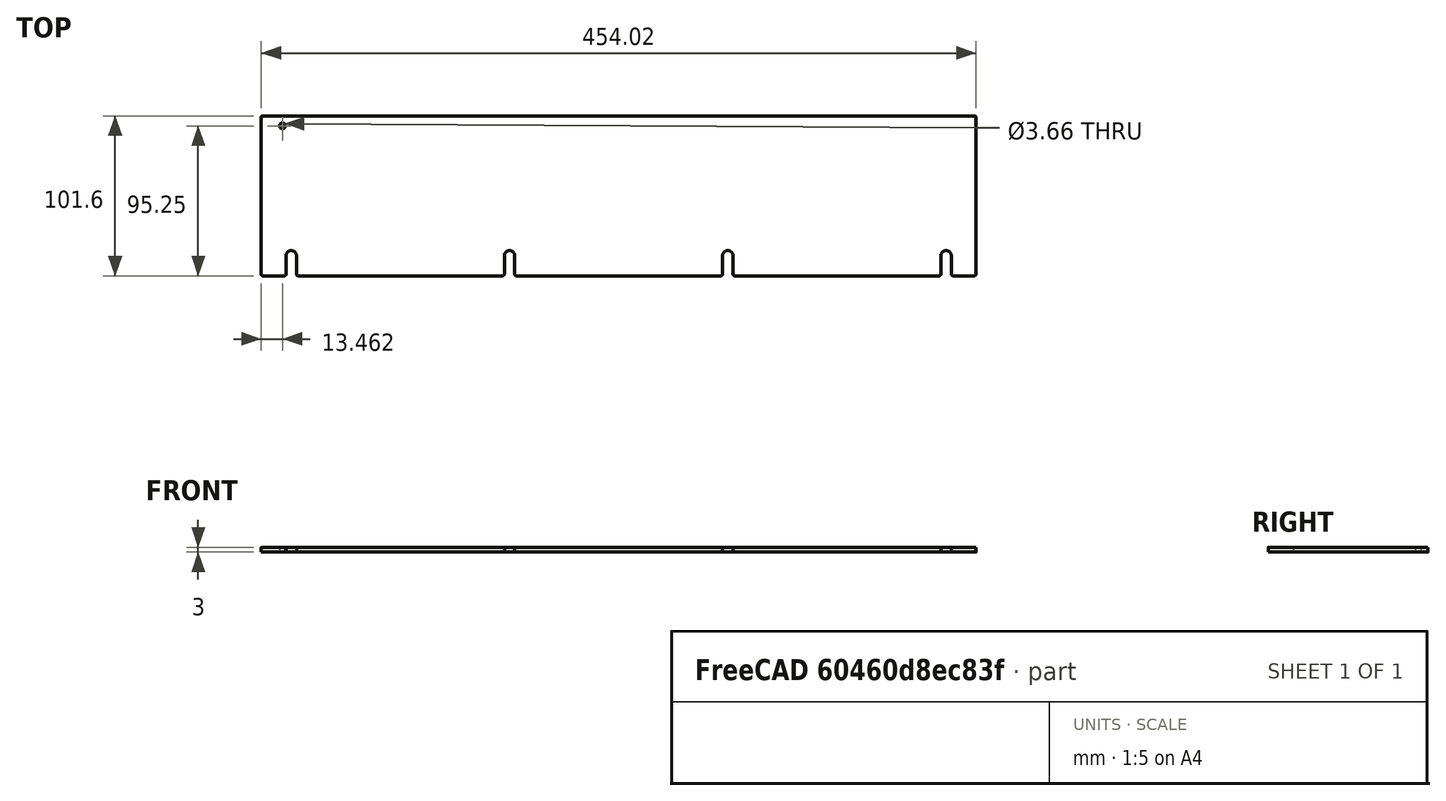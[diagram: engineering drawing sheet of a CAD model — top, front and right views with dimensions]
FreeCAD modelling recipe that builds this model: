
FCSTD DOCUMENT  (FreeCAD 0.21R33675 (Git))
Label: plain_wall_17p875in
License: All rights reserved
LicenseURL: http://en.wikipedia.org/wiki/All_rights_reserved
objects: Sketcher::SketchObject×1, Spreadsheet::Sheet×1, PartDesign::Pad×1, PartDesign::Body×1
note: 4 computed .brp shape members not serialized (recipe doc carries the construction recipe); baked Part::Feature solids carry a one-line shape summary decoded from their .brp

FEATURE [Sketcher::SketchObject] Sketch
  FullyConstrained = true
  MapMode = 5
  Support = -> [XY_Plane]
  expr: Constraints[125] = Spreadsheet.BracketHoleFromSide
  expr: Constraints[126] = Spreadsheet.UpperBracketHoleFromTop
  expr: Constraints[127] = Spreadsheet.BracketHoleDiameter
  expr: Constraints[19] = Spreadsheet.FilletRadius
  expr: Constraints[21] = Spreadsheet.Height
  expr: Constraints[22] = Spreadsheet.Length
  expr: Constraints[27] = Spreadsheet.MountHoleDistanceFromBottom
  expr: Constraints[29] = Spreadsheet.MountHoleDiameter
  expr: Constraints[49] = Spreadsheet.MountHoleSideMargin
  expr: Constraints[53] = Spreadsheet.MountHoleDistanceFromBottom
  sketch-geometry (49):
    g0: ArcOfCircle CenterX=-226.012 CenterY=49.8 CenterZ=0 NormalX=0 NormalY=0 NormalZ=1 AngleXU=0 Radius=1 StartAngle=1.5708 EndAngle=3.14159
    g1: LineSegment StartX=-226.012 StartY=50.8 StartZ=0 EndX=226.012 EndY=50.8 EndZ=0
    g2: ArcOfCircle CenterX=226.012 CenterY=49.8 CenterZ=0 NormalX=0 NormalY=0 NormalZ=1 AngleXU=0 Radius=1 StartAngle=-2.7e-15 EndAngle=1.5708
    g3: LineSegment StartX=227.012 StartY=49.8 StartZ=0 EndX=227.012 EndY=-49.8 EndZ=0
    g4: ArcOfCircle CenterX=226.012 CenterY=-49.8 CenterZ=0 NormalX=0 NormalY=0 NormalZ=1 AngleXU=0 Radius=1 StartAngle=4.71239 EndAngle=6.28319
    g5: LineSegment StartX=226.012 StartY=-50.8 StartZ=0 EndX=-226.012 EndY=-50.8 EndZ=0
    g6: ArcOfCircle CenterX=-226.012 CenterY=-49.8 CenterZ=0 NormalX=0 NormalY=0 NormalZ=1 AngleXU=0 Radius=1 StartAngle=3.14159 EndAngle=4.71239
    g7: LineSegment StartX=-227.012 StartY=-49.8 StartZ=0 EndX=-227.012 EndY=49.8 EndZ=0
    g8: GeomPoint X=-227.012 Y=50.8 Z=0
    g9: GeomPoint X=227.013 Y=-50.8 Z=0
    g10: LineSegment StartX=-69.3208 StartY=-38.1 StartZ=0 EndX=69.3208 EndY=-38.1 EndZ=0
    g11: LineSegment StartX=0 StartY=-50.8 StartZ=0 EndX=0 EndY=-38.1 EndZ=0
    g12: Circle CenterX=-69.3208 CenterY=-38.1 CenterZ=0 NormalX=0 NormalY=0 NormalZ=1 AngleXU=0 Radius=3.302
    g13: Circle CenterX=69.3208 CenterY=-38.1 CenterZ=0 NormalX=0 NormalY=0 NormalZ=1 AngleXU=0 Radius=3.302
    g14: LineSegment StartX=-69.3208 StartY=-38.1 StartZ=0 EndX=-207.963 EndY=-38.1 EndZ=0
    g15: LineSegment StartX=-207.963 StartY=-38.1 StartZ=0 EndX=-227.012 EndY=-38.1 EndZ=0
    g16: LineSegment StartX=69.3208 StartY=-38.1 StartZ=0 EndX=207.963 EndY=-38.1 EndZ=0
    g17: LineSegment StartX=207.963 StartY=-38.1 StartZ=0 EndX=227.013 EndY=-38.1 EndZ=0
    g18: Circle CenterX=-207.963 CenterY=-38.1 CenterZ=0 NormalX=0 NormalY=0 NormalZ=1 AngleXU=0 Radius=3.302
    g19: Circle CenterX=207.963 CenterY=-38.1 CenterZ=0 NormalX=0 NormalY=0 NormalZ=1 AngleXU=0 Radius=3.302
    g20: LineSegment StartX=0 StartY=-38.1 StartZ=0 EndX=0 EndY=-50.8 EndZ=0
    g21: ArcOfCircle CenterX=-207.963 CenterY=-38.1 CenterZ=0 NormalX=0 NormalY=0 NormalZ=1 AngleXU=0 Radius=3.302 StartAngle=-2.7e-15 EndAngle=3.14159
    g22: LineSegment StartX=-211.264 StartY=-38.1 StartZ=0 EndX=-211.264 EndY=-49.8 EndZ=0
    g23: LineSegment StartX=-204.661 StartY=-38.1 StartZ=0 EndX=-204.661 EndY=-49.8 EndZ=0
    g24: ArcOfCircle CenterX=-212.264 CenterY=-49.8 CenterZ=0 NormalX=0 NormalY=0 NormalZ=1 AngleXU=0 Radius=1 StartAngle=4.71239 EndAngle=6.28319
    g25: ArcOfCircle CenterX=-203.66 CenterY=-49.8 CenterZ=0 NormalX=0 NormalY=0 NormalZ=1 AngleXU=0 Radius=1 StartAngle=3.14159 EndAngle=4.71239
    g26: ArcOfCircle CenterX=-69.3208 CenterY=-38.1 CenterZ=0 NormalX=0 NormalY=0 NormalZ=1 AngleXU=0 Radius=3.302 StartAngle=0 EndAngle=3.14159
    g27: LineSegment StartX=-72.6228 StartY=-38.1 StartZ=0 EndX=-72.6228 EndY=-49.8 EndZ=0
    g28: LineSegment StartX=-66.0188 StartY=-38.1 StartZ=0 EndX=-66.0188 EndY=-49.8 EndZ=0
    g29: ArcOfCircle CenterX=-73.6228 CenterY=-49.8 CenterZ=0 NormalX=0 NormalY=0 NormalZ=1 AngleXU=0 Radius=1 StartAngle=4.71239 EndAngle=6.28319
    g30: ArcOfCircle CenterX=-65.0188 CenterY=-49.8 CenterZ=0 NormalX=0 NormalY=0 NormalZ=1 AngleXU=0 Radius=1 StartAngle=3.14159 EndAngle=4.71239
    g31: ArcOfCircle CenterX=69.3208 CenterY=-38.1 CenterZ=0 NormalX=0 NormalY=0 NormalZ=1 AngleXU=0 Radius=3.302 StartAngle=-9e-16 EndAngle=3.14159
    g32: LineSegment StartX=66.0188 StartY=-38.1 StartZ=0 EndX=66.0188 EndY=-49.8 EndZ=0
    g33: LineSegment StartX=72.6228 StartY=-38.1 StartZ=0 EndX=72.6228 EndY=-49.8 EndZ=0
    g34: ArcOfCircle CenterX=65.0188 CenterY=-49.8 CenterZ=0 NormalX=0 NormalY=0 NormalZ=1 AngleXU=0 Radius=1 StartAngle=4.71239 EndAngle=6.28319
    g35: ArcOfCircle CenterX=73.6228 CenterY=-49.8 CenterZ=0 NormalX=0 NormalY=0 NormalZ=1 AngleXU=0 Radius=1 StartAngle=3.14159 EndAngle=4.71239
    g36: ArcOfCircle CenterX=207.963 CenterY=-38.1 CenterZ=0 NormalX=0 NormalY=0 NormalZ=1 AngleXU=0 Radius=3.302 StartAngle=1.27e-14 EndAngle=3.14159
    g37: LineSegment StartX=204.661 StartY=-38.1 StartZ=0 EndX=204.661 EndY=-49.8 EndZ=0
    g38: LineSegment StartX=211.264 StartY=-38.1 StartZ=0 EndX=211.264 EndY=-49.8 EndZ=0
    g39: ArcOfCircle CenterX=203.661 CenterY=-49.8 CenterZ=0 NormalX=0 NormalY=0 NormalZ=1 AngleXU=0 Radius=1 StartAngle=4.71239 EndAngle=6.28319
    g40: ArcOfCircle CenterX=212.264 CenterY=-49.8 CenterZ=0 NormalX=0 NormalY=0 NormalZ=1 AngleXU=0 Radius=1 StartAngle=3.14159 EndAngle=4.71239
    g41: LineSegment StartX=212.264 StartY=-50.8 StartZ=0 EndX=226.012 EndY=-50.8 EndZ=0
    g42: LineSegment StartX=203.661 StartY=-50.8 StartZ=0 EndX=73.6228 EndY=-50.8 EndZ=0
    g43: LineSegment StartX=65.0188 StartY=-50.8 StartZ=0 EndX=-65.0188 EndY=-50.8 EndZ=0
    g44: LineSegment StartX=-73.6228 StartY=-50.8 StartZ=0 EndX=-203.66 EndY=-50.8 EndZ=0
    g45: LineSegment StartX=-212.264 StartY=-50.8 StartZ=0 EndX=-226.012 EndY=-50.8 EndZ=0
    g46: LineSegment StartX=-227.012 StartY=50.8 StartZ=0 EndX=-213.548 EndY=50.8 EndZ=0
    g47: LineSegment StartX=-213.548 StartY=50.8 StartZ=0 EndX=-213.548 EndY=44.45 EndZ=0
    g48: Circle CenterX=-213.548 CenterY=44.45 CenterZ=0 NormalX=0 NormalY=0 NormalZ=1 AngleXU=0 Radius=1.8288
  constraints (128):
    c: Tangent(g0,g1) = 1.5708
    c: Tangent(g1,g2) = 1.5708
    c: Tangent(g2,g3) = 1.5708
    c: Tangent(g3,g4) = 1.5708
    c: Tangent(g4,g5) = 1.5708
    c: Tangent(g5,g6) = 1.5708
    c: Tangent(g6,g7) = 1.5708
    c: Tangent(g7,g0) = 1.5708
    c: Horizontal(g1)
    c: Horizontal(g5)
    c: Vertical(g3)
    c: Vertical(g7)
    c: Equal(g0,g2)
    c: Equal(g2,g4)
    c: Equal(g4,g6)
    c: PointOnObject(g8,g1)
    c: PointOnObject(g8,g7)
    c: PointOnObject(g9,g3)
    c: PointOnObject(g9,g5)
    c: Radius(g2) = 1
    c: Symmetric(g8,g9,g-1)
    c: DistanceY(g4,g1) = 101.6
    c: DistanceX(g0,g2) = 454.025
    c: Horizontal(g10)
    c: Vertical(g11)
    c: PointOnObject(g11,g5)
    c: PointOnObject(g11,g-2)
    c: DistanceY(g11,g11) = 12.7
    c: Coincident(g13,g10)
    c: Diameter(g13) = 6.604
    c: Equal(g12,g13)
    c: Coincident(g12,g10)
    c: Coincident(g14,g12)
    c: Horizontal(g14)
    c: Coincident(g15,g14)
    c: PointOnObject(g15,g7)
    c: Horizontal(g15)
    c: Coincident(g16,g13)
    c: Horizontal(g16)
    c: Coincident(g17,g16)
    c: PointOnObject(g17,g3)
    c: Horizontal(g17)
    c: Equal(g17,g15)
    c: Equal(g14,g10)
    c: Equal(g10,g16)
    c: Coincident(g18,g14)
    c: Coincident(g19,g16)
    c: Equal(g18,g12)
    c: Equal(g13,g19)
    c: DistanceX(g15,g15) = 19.05
    c: PointOnObject(g20,g10)
    c: Vertical(g20)
    c: Coincident(g20,g11)
    c: DistanceY(g20,g20) = 12.7
    c: Coincident(g21,g14)
    c: PointOnObject(g21,g15)
    c: PointOnObject(g21,g14)
    c: PointOnObject(g21,g18)
    c: Coincident(g22,g21)
    c: Vertical(g22)
    c: Coincident(g23,g21)
    c: Vertical(g23)
    c: Equal(g22,g23)
    c: Tangent(g24,g22) = 1.5708
    c: Tangent(g24,g5) = 1.5708
    c: Tangent(g25,g23) = -1.5708
    c: Tangent(g25,g5) = 1.5708
    c: Equal(g24,g6)
    c: Coincident(g26,g10)
    c: PointOnObject(g26,g14)
    c: PointOnObject(g26,g10)
    c: PointOnObject(g26,g12)
    c: Coincident(g27,g26)
    c: Vertical(g27)
    c: Coincident(g28,g26)
    c: Vertical(g28)
    c: Equal(g27,g28)
    c: Tangent(g29,g27) = 1.5708
    c: Tangent(g29,g5) = 1.5708
    c: Tangent(g30,g28) = -1.5708
    c: Tangent(g30,g5) = 1.5708
    c: Equal(g29,g6)
    c: Coincident(g31,g10)
    c: PointOnObject(g31,g10)
    c: PointOnObject(g31,g16)
    c: PointOnObject(g31,g13)
    c: Coincident(g32,g31)
    c: Vertical(g32)
    c: Coincident(g33,g31)
    c: Vertical(g33)
    c: Equal(g32,g33)
    c: Tangent(g34,g32) = 1.5708
    c: Tangent(g34,g5) = 1.5708
    c: Tangent(g35,g33) = -1.5708
    c: Tangent(g35,g5) = 1.5708
    c: Equal(g34,g4)
    c: Coincident(g36,g16)
    c: PointOnObject(g36,g16)
    c: PointOnObject(g36,g17)
    c: PointOnObject(g36,g19)
    c: Coincident(g37,g36)
    c: Vertical(g37)
    c: Coincident(g38,g36)
    c: Vertical(g38)
    c: Equal(g37,g38)
    c: Tangent(g39,g37) = 1.5708
    c: Tangent(g39,g5) = 1.5708
    c: Tangent(g40,g38) = -1.5708
    c: Tangent(g40,g5) = 1.5708
    c: Equal(g40,g4)
    c: Coincident(g41,g40)
    c: Coincident(g41,g4)
    c: Coincident(g42,g39)
    c: Coincident(g42,g35)
    c: Coincident(g43,g34)
    c: Coincident(g43,g30)
    c: Coincident(g44,g29)
    c: Coincident(g25,g44)
    c: Coincident(g45,g24)
    c: Coincident(g45,g6)
    c: Horizontal(g46)
    c: Coincident(g8,g46)
    c: Coincident(g47,g46)
    c: Vertical(g47)
    c: Coincident(g48,g47)
    c: DistanceX(g46,g46) = 13.4648
    c: DistanceY(g47,g47) = 6.35
    c: Diameter(g48) = 3.6576
FEATURE [Spreadsheet::Sheet] Spreadsheet
  cells = A2='Parameters; A3='Height; B3(Height)==4 in; A4='Length; B4(Length)==17.875 in; A5='Thickness; B5(Thickness)==3 mm; A6='FilletRadius; B6(FilletRadius)==1 mm; A7='MountHoleDiameter; B7(MountHoleDiameter)==0.26 in; A8='MountHoleDistanceFromBottom; B8(MountHoleDistanceFromBottom)==0.5 in; A9='MountHoleSideMargin; B9(MountHoleSideMargin)==0.75 in; A11='BracketWidth; B11(BracketWidth)==0.5 in; A12='BracketHoleDiameter; B12(BracketHoleDiameter)==0.144 in; A13='BracketHoleOffset; B13(BracketHoleOffset)==0.412 in; A14='UpperBracketHoleFromTop; B14(UpperBracketHoleFromTop)==0.5 * BracketWidth; A15='BracketHoleFromSide; B15(BracketHoleFromSide)==BracketHoleOffset + Thickness
FEATURE [PartDesign::Pad] Pad
  Direction = (0,0,1)
  Length = 3
  Length2 = 10
  Profile = -> Sketch
  ReferenceAxis = -> Sketch [N_Axis]
  Type = 0
  expr: Length = Spreadsheet.Thickness
FEATURE [PartDesign::Body] Body
  Group = -> [Sketch,Pad]
  Origin = -> Origin
  Tip = -> Pad
